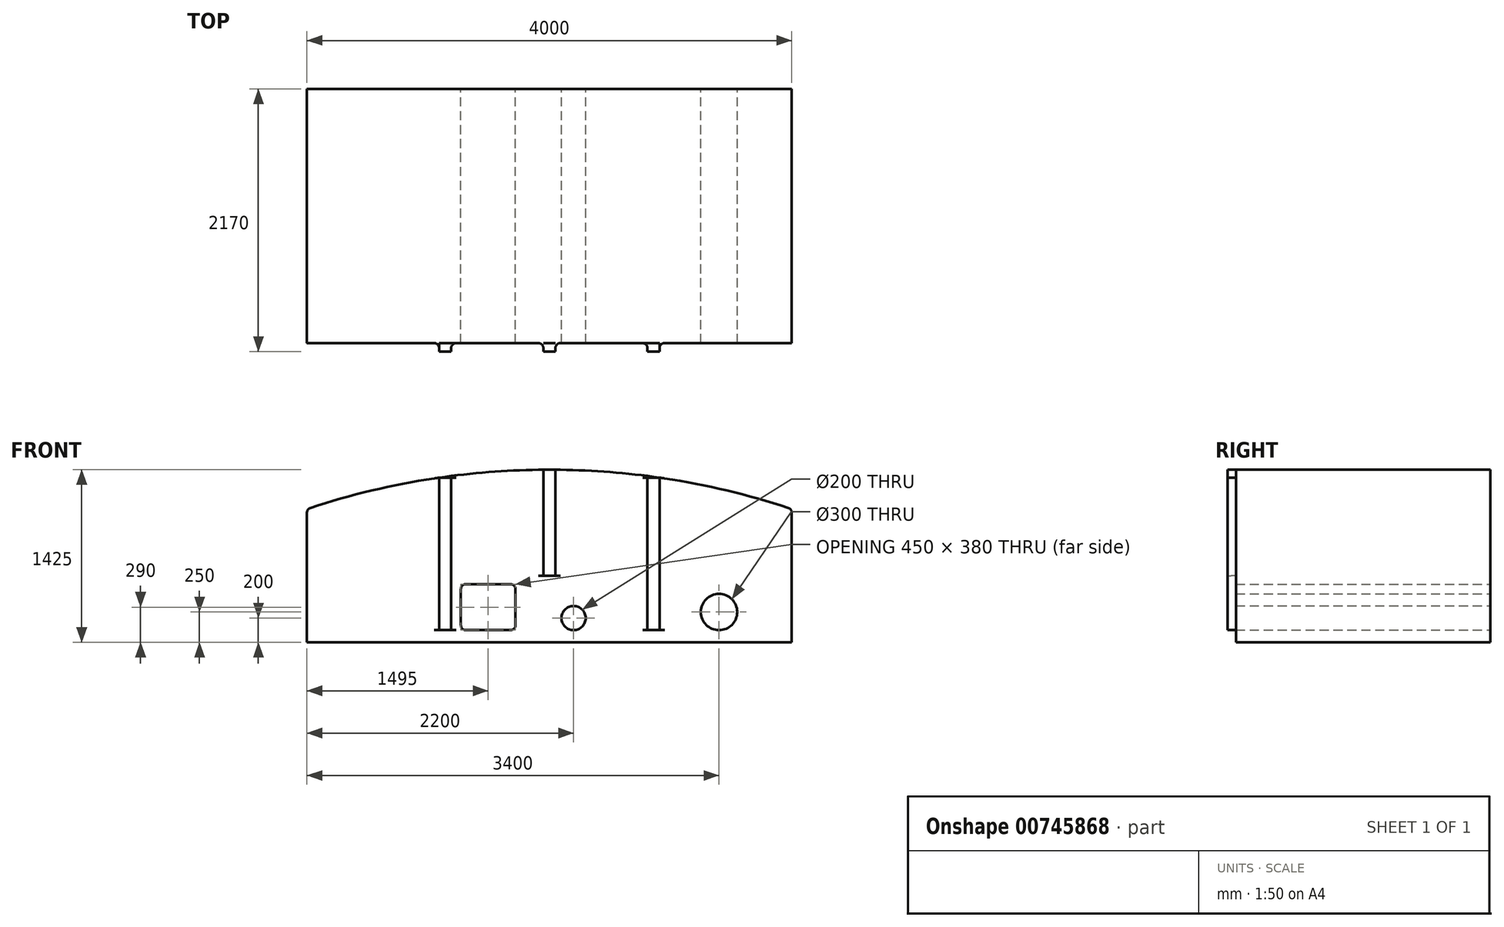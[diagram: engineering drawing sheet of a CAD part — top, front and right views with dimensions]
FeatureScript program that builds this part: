
annotation { "Feature Type Name" : "Feature", "Feature Type Description" : "" }
export const myFeature = defineFeature(function(context is Context, id is Id, definition is map)
    precondition{}
    {
        {
            var Q0;
            Q0=qCreatedBy(makeId("Front.planeOp"),FACE);
            var sketch = newSketch(context, id + "F0", { "sketchPlane" : qUnion([Q0])});
            skLineSegment(sketch, "E0.bottom", {"start": v(2000, -550) * mm, "end": v(-2000, -550) * mm});
            skLineSegment(sketch, "E0.left", {"start": v(2000, -550) * mm, "end": v(2000, 550) * mm});
            skLineSegment(sketch, "E0.right", {"start": v(-2000, -550) * mm, "end": v(-2000, 550) * mm});
            skPoint(sketch, "E0.middle", {"position": v(0, 0) * mm});
            skArc(sketch, "E1", {"start": v(2000, 550) * mm, "mid": v(0, 875) * mm, "end": v(-2000, 550) * mm});
            skLineSegment(sketch, "E2.bottom", {"start": v(-730, -70) * mm, "end": v(-280, -70) * mm});
            skLineSegment(sketch, "E2.top", {"start": v(-730, -450) * mm, "end": v(-280, -450) * mm});
            skLineSegment(sketch, "E2.left", {"start": v(-730, -70) * mm, "end": v(-730, -450) * mm});
            skLineSegment(sketch, "E2.right", {"start": v(-280, -70) * mm, "end": v(-280, -450) * mm});
            skCircle(sketch, "E3", {"center": v(200, -350) * mm, "radius": 100 * mm});
            skCircle(sketch, "E4", {"center": v(1400, -300) * mm, "radius": 150 * mm});
            skPoint(sketch, "E5", {"position": v(0, -550) * mm});
            skSolve(sketch);
        }
        {
            var Q0;
            Q0=makeQuery(id+"F0.imprint","IMPRINT",FACE,{"disambiguationData":[TD([[makeQuery(id+"F0.imprint","IMPRINT",EDGE,{"derivedFrom":sQuery(id+"F0.wireOp",EDGE,"E0.bottom")}),-1.0]])]});
            extrude(context, id + "F1", {"entities" : qUnion([Q0]), "endBound" : BoundingType.SYMMETRIC, "depth" : 2100 * mm, "offsetDistance" : 25 * mm});
        }
        {
            var Q0;
            Q0=makeQuery(id+"F1.opExtrude","CAP_FACE",FACE,{"disambiguationData":[OSD([sQuery(id+"F0.wireOp",EDGE,"E0.bottom"),sQuery(id+"F0.wireOp",EDGE,"E0.left"),sQuery(id+"F0.wireOp",EDGE,"E0.right"),sQuery(id+"F0.wireOp",EDGE,"E1"),sQuery(id+"F0.wireOp",EDGE,"E2.bottom"),sQuery(id+"F0.wireOp",EDGE,"E2.top"),sQuery(id+"F0.wireOp",EDGE,"E2.left"),sQuery(id+"F0.wireOp",EDGE,"E2.right"),sQuery(id+"F0.wireOp",EDGE,"E3"),sQuery(id+"F0.wireOp",EDGE,"E4")])],"isStart":false});
            var sketch = newSketch(context, id + "F2", { "sketchPlane" : qUnion([Q0])});
            skLineSegment(sketch, "E6.bottom", {"start": v(-910, 809.1) * mm, "end": v(-810, 809.1) * mm});
            skLineSegment(sketch, "E6.top", {"start": v(-910, -450) * mm, "end": v(-810, -450) * mm});
            skLineSegment(sketch, "E6.left", {"start": v(-910, 809.1) * mm, "end": v(-910, -450) * mm});
            skLineSegment(sketch, "E6.right", {"start": v(-810, 809.1) * mm, "end": v(-810, -450) * mm});
            skLineSegment(sketch, "E7.bottom", {"start": v(-50, 874.8) * mm, "end": v(50, 874.8) * mm});
            skLineSegment(sketch, "E7.top", {"start": v(-50, 0) * mm, "end": v(50, 0) * mm});
            skLineSegment(sketch, "E7.left", {"start": v(-50, 874.8) * mm, "end": v(-50, 0) * mm});
            skLineSegment(sketch, "E7.right", {"start": v(50, 874.8) * mm, "end": v(50, 0) * mm});
            skLineSegment(sketch, "E8.bottom", {"start": v(810, 809.1) * mm, "end": v(910, 809.1) * mm});
            skLineSegment(sketch, "E8.top", {"start": v(810, -450) * mm, "end": v(910, -450) * mm});
            skLineSegment(sketch, "E8.left", {"start": v(910, 809.1) * mm, "end": v(910, -450) * mm});
            skLineSegment(sketch, "E8.right", {"start": v(810, 809.1) * mm, "end": v(810, -450) * mm});
            skPoint(sketch, "E9", {"position": v(0, 0) * mm});
            skSolve(sketch);
        }
        {
            var Q0;
            Q0 = qSketchRegion(id + "F2", true);
            extrude(context, id + "F3", {"entities" : qUnion([Q0]), "operationType" : NewBodyOperationType.ADD, "depth" : 70 * mm, "offsetDistance" : 25 * mm});
        }
        {
            var Q0;
            Q0=makeQuery(id+"F1.opExtrude","SWEPT_EDGE",EDGE,{"disambiguationData":[OSD([sQuery(id+"F0.wireOp",EDGE,"E2.top"),sQuery(id+"F0.wireOp",EDGE,"E2.left")])]});
            var Q1;
            Q1=makeQuery(id+"F1.opExtrude","SWEPT_EDGE",EDGE,{"disambiguationData":[OSD([sQuery(id+"F0.wireOp",EDGE,"E2.bottom"),sQuery(id+"F0.wireOp",EDGE,"E2.left")])]});
            var Q2;
            Q2=makeQuery(id+"F1.opExtrude","SWEPT_EDGE",EDGE,{"disambiguationData":[OSD([sQuery(id+"F0.wireOp",EDGE,"E2.top"),sQuery(id+"F0.wireOp",EDGE,"E2.right")])]});
            var Q3;
            Q3=makeQuery(id+"F1.opExtrude","SWEPT_EDGE",EDGE,{"disambiguationData":[OSD([sQuery(id+"F0.wireOp",EDGE,"E2.bottom"),sQuery(id+"F0.wireOp",EDGE,"E2.right")])]});
            var Q4;
            Q4=makeQuery(id+"F3.opExtrude","CAP_EDGE",EDGE,{"disambiguationData":[OSD([sQuery(id+"F2.wireOp",EDGE,"E8.left")])],"isStart":true});
            var Q5;
            Q5=makeQuery(id+"F3.opExtrude","CAP_EDGE",EDGE,{"disambiguationData":[OSD([sQuery(id+"F2.wireOp",EDGE,"E7.right")])],"isStart":true});
            var Q6;
            Q6=makeQuery(id+"F3.opExtrude","CAP_EDGE",EDGE,{"disambiguationData":[OSD([sQuery(id+"F2.wireOp",EDGE,"E7.left")])],"isStart":true});
            var Q7;
            Q7=makeQuery(id+"F3.opExtrude","CAP_EDGE",EDGE,{"disambiguationData":[OSD([sQuery(id+"F2.wireOp",EDGE,"E6.right")])],"isStart":true});
            var Q8;
            Q8=makeQuery(id+"F3.opExtrude","CAP_EDGE",EDGE,{"disambiguationData":[OSD([sQuery(id+"F2.wireOp",EDGE,"E6.left")])],"isStart":true});
            var Q9;
            Q9=makeQuery(id+"F3.opExtrude","CAP_EDGE",EDGE,{"disambiguationData":[OSD([sQuery(id+"F2.wireOp",EDGE,"E8.right")])],"isStart":true});
            var Q10;
            Q10=makeQuery(id+"F1.opExtrude","SWEPT_EDGE",EDGE,{"disambiguationData":[OSD([sQuery(id+"F0.wireOp",EDGE,"E0.left"),sQuery(id+"F0.wireOp",EDGE,"E1")])]});
            var Q11;
            Q11=makeQuery(id+"F1.opExtrude","SWEPT_EDGE",EDGE,{"disambiguationData":[OSD([sQuery(id+"F0.wireOp",EDGE,"E0.right"),sQuery(id+"F0.wireOp",EDGE,"E1")])]});
            fillet(context, id + "F4", {"entities" : qUnion([Q0, Q1, Q2, Q3, Q4, Q5, Q6, Q7, Q8, Q9, Q10, Q11]), "radius" : 40 * mm, "tangentPropagation" : true, "allowEdgeOverflow" : false});
        }
    });
